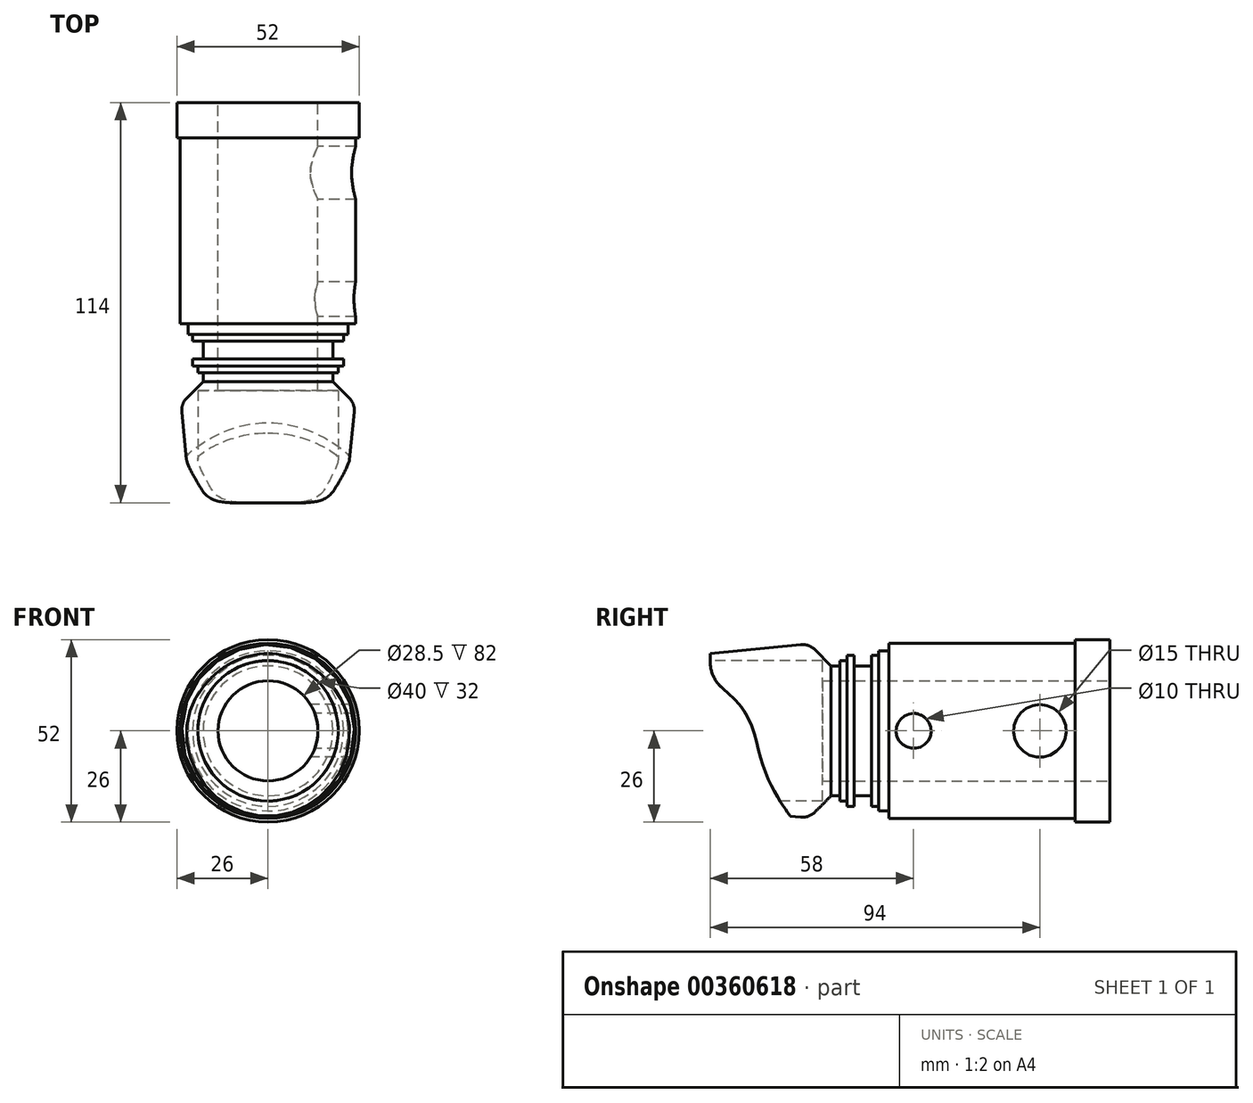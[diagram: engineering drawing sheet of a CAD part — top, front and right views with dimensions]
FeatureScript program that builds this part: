
annotation { "Feature Type Name" : "Feature", "Feature Type Description" : "" }
export const myFeature = defineFeature(function(context is Context, id is Id, definition is map)
    precondition{}
    {
        {
            var Q0;
            Q0=qCreatedBy(makeId("Front.planeOp"),FACE);
            var sketch = newSketch(context, id + "F0", { "sketchPlane" : qUnion([Q0])});
            skCircle(sketch, "E0", {"center": v(0, 0) * mm, "radius": 25 * mm});
            skSolve(sketch);
        }
        {
            var Q0;
            Q0 = qSketchRegion(id + "F0", true);
            extrude(context, id + "F1", {"entities" : qUnion([Q0]), "depth" : 53 * mm});
        }
        {
            var Q0;
            Q0=makeQuery(id+"F1.opExtrude","CAP_FACE",FACE,{"disambiguationData":[OSD([sQuery(id+"F0.wireOp",EDGE,"E0")])],"isStart":true});
            var sketch = newSketch(context, id + "F2", { "sketchPlane" : qUnion([Q0])});
            skCircle(sketch, "E1", {"center": v(0, 0) * mm, "radius": 26 * mm});
            skSolve(sketch);
        }
        {
            var Q0;
            Q0 = qSketchRegion(id + "F2", true);
            extrude(context, id + "F3", {"entities" : qUnion([Q0]), "operationType" : NewBodyOperationType.ADD, "depth" : 10 * mm});
        }
        {
            var Q0;
            Q0=makeQuery(id+"F1.opExtrude","CAP_FACE",FACE,{"disambiguationData":[OSD([sQuery(id+"F0.wireOp",EDGE,"E0")])],"isStart":false});
            var sketch = newSketch(context, id + "F4", { "sketchPlane" : qUnion([Q0])});
            skCircle(sketch, "E2", {"center": v(0, 0) * mm, "radius": 22.83 * mm});
            skSolve(sketch);
        }
        {
            var Q0;
            Q0 = qSketchRegion(id + "F4", true);
            extrude(context, id + "F5", {"entities" : qUnion([Q0]), "operationType" : NewBodyOperationType.ADD, "depth" : 3 * mm});
        }
        {
            var Q0;
            Q0=makeQuery(id+"F5.opExtrude","CAP_FACE",FACE,{"disambiguationData":[OSD([sQuery(id+"F4.wireOp",EDGE,"E2")])],"isStart":false});
            var sketch = newSketch(context, id + "F6", { "sketchPlane" : qUnion([Q0])});
            skCircle(sketch, "E3", {"center": v(0, 0) * mm, "radius": 21.5 * mm});
            skSolve(sketch);
        }
        {
            var Q0;
            Q0=makeQuery(id+"F6.imprint","IMPRINT",FACE,{"disambiguationData":[TD([[makeQuery(id+"F6.imprint","IMPRINT",EDGE,{"derivedFrom":sQuery(id+"F6.wireOp",EDGE,"E3")}),1.0]])]});
            extrude(context, id + "F7", {"entities" : qUnion([Q0]), "operationType" : NewBodyOperationType.ADD, "depth" : 2 * mm});
        }
        {
            var Q0;
            Q0=makeQuery(id+"F7.opExtrude","CAP_FACE",FACE,{"disambiguationData":[OSD([sQuery(id+"F6.wireOp",EDGE,"E3")])],"isStart":false});
            var sketch = newSketch(context, id + "F8", { "sketchPlane" : qUnion([Q0])});
            skCircle(sketch, "E4", {"center": v(0, 0) * mm, "radius": 18.5 * mm});
            skSolve(sketch);
        }
        {
            var Q0;
            Q0=makeQuery(id+"F8.imprint","IMPRINT",FACE,{"disambiguationData":[TD([[makeQuery(id+"F8.imprint","IMPRINT",EDGE,{"derivedFrom":sQuery(id+"F8.wireOp",EDGE,"E4")}),1.0]])]});
            extrude(context, id + "F9", {"entities" : qUnion([Q0]), "operationType" : NewBodyOperationType.ADD, "depth" : 5 * mm});
        }
        {
            var Q0;
            Q0=makeQuery(id+"F9.opExtrude","CAP_FACE",FACE,{"disambiguationData":[OSD([sQuery(id+"F8.wireOp",EDGE,"E4")])],"isStart":false});
            var sketch = newSketch(context, id + "F10", { "sketchPlane" : qUnion([Q0])});
            skCircle(sketch, "E5", {"center": v(0, 0) * mm, "radius": 21.5 * mm});
            skSolve(sketch);
        }
        {
            var Q0;
            Q0 = qSketchRegion(id + "F10", true);
            extrude(context, id + "F11", {"entities" : qUnion([Q0]), "operationType" : NewBodyOperationType.ADD, "depth" : 2 * mm});
        }
        {
            var Q0;
            Q0=makeQuery(id+"F11.opExtrude","CAP_FACE",FACE,{"disambiguationData":[OSD([sQuery(id+"F10.wireOp",EDGE,"E5")])],"isStart":false});
            var sketch = newSketch(context, id + "F12", { "sketchPlane" : qUnion([Q0])});
            skCircle(sketch, "E6", {"center": v(0, 0) * mm, "radius": 20 * mm});
            skSolve(sketch);
        }
        {
            var Q0;
            Q0 = qSketchRegion(id + "F12", true);
            extrude(context, id + "F13", {"entities" : qUnion([Q0]), "operationType" : NewBodyOperationType.ADD, "depth" : 2 * mm});
        }
        {
            var Q0;
            Q0=makeQuery(id+"F13.opExtrude","CAP_FACE",FACE,{"disambiguationData":[OSD([sQuery(id+"F12.wireOp",EDGE,"E6")])],"isStart":false});
            var sketch = newSketch(context, id + "F14", { "sketchPlane" : qUnion([Q0])});
            skCircle(sketch, "E7", {"center": v(0, 0) * mm, "radius": 18.5 * mm});
            skSolve(sketch);
        }
        {
            var Q0;
            Q0 = qSketchRegion(id + "F14", true);
            extrude(context, id + "F15", {"entities" : qUnion([Q0]), "operationType" : NewBodyOperationType.ADD, "depth" : 2 * mm});
        }
        {
            var Q0;
            Q0=makeQuery(id+"F15.opExtrude","CAP_FACE",FACE,{"disambiguationData":[OSD([sQuery(id+"F14.wireOp",EDGE,"E7")])],"isStart":false});
            var sketch = newSketch(context, id + "F16", { "sketchPlane" : qUnion([Q0])});
            skCircle(sketch, "E8", {"center": v(0, 0) * mm, "radius": 25 * mm});
            skSolve(sketch);
        }
        {
            var Q0;
            Q0 = qSketchRegion(id + "F16", true);
            extrude(context, id + "F17", {"entities" : qUnion([Q0]), "operationType" : NewBodyOperationType.ADD, "depth" : 35 * mm});
        }
        {
            var Q0;
            Q0=makeQuery(id+"F17.opExtrude","CAP_FACE",FACE,{"disambiguationData":[OSD([sQuery(id+"F16.wireOp",EDGE,"E8")])],"isStart":false});
            var sketch = newSketch(context, id + "F18", { "sketchPlane" : qUnion([Q0])});
            skCircle(sketch, "E9", {"center": v(0, 0) * mm, "radius": 20 * mm});
            skSolve(sketch);
        }
        {
            var Q0;
            Q0 = qSketchRegion(id + "F18", true);
            extrude(context, id + "F19", {"entities" : qUnion([Q0]), "operationType" : NewBodyOperationType.REMOVE, "oppositeDirection" : true, "depth" : 32 * mm});
        }
        {
            var Q0;
            Q0=makeQuery(id+"F17.opExtrude","CAP_EDGE",EDGE,{"disambiguationData":[OSD([sQuery(id+"F16.wireOp",EDGE,"E8")])],"isStart":true});
            chamfer(context, id + "F20", {"entities" : qUnion([Q0]), "width" : 7 * mm, "tangentPropagation" : true});
        }
        {
            var Q0;
            Q0=makeQuery(id+"F17.opExtrude","CAP_EDGE",EDGE,{"disambiguationData":[OSD([sQuery(id+"F16.wireOp",EDGE,"E8")])],"isStart":false});
            chamfer(context, id + "F21", {"entities" : qUnion([Q0]), "chamferType" : ChamferType.TWO_OFFSETS, "width1" : 3 * mm, "oppositeDirection" : false, "width2" : 30 * mm, "tangentPropagation" : true});
        }
        {
            var Q0;
            {var subQ0=sQuery(id+"F16.wireOp",EDGE,"E8");Q0=makeQuery(id+"F21.opChamfer","BLEND_EDGE",EDGE,{"blendedFrom":[makeQuery(id+"F17.opExtrude","CAP_EDGE",EDGE,{"disambiguationData":[OSD([subQ0])],"isStart":false}),makeQuery(id+"F20.opChamfer","BLEND_FACE",FACE,{"disambiguationData":[OSD([subQ0])]})],"blendedInto":[makeQuery(id+"F20.opChamfer","BLEND_FACE",FACE,{"disambiguationData":[OSD([subQ0])]})]});}
            fillet(context, id + "F22", {"entities" : qUnion([Q0]), "radius" : 5 * mm, "tangentPropagation" : true, "allowEdgeOverflow" : false});
        }
        {
            var Q0;
            Q0=qCreatedBy(makeId("Right.planeOp"),FACE);
            cPlane(context, id + "F23", {"entities" : qUnion([Q0]), "cplaneType" : CPlaneType.OFFSET, "offset" : 26.9 * mm, "width" : 150 * mm, "height" : 150 * mm});
        }
        {
            var Q0;
            Q0=qCreatedBy(id+"F23.planeOp",FACE);
            var sketch = newSketch(context, id + "F24", { "sketchPlane" : qUnion([Q0])});
            skLineSegment(sketch, "E10", {"start": v(0, 0) * mm, "end": v(-78, 0) * mm});
            skLineSegment(sketch, "E11", {"start": v(-78, 0) * mm, "end": v(-78, -31.05) * mm});
            skFitSpline(sketch, "E12", {"points": [v(-78, -28.4) * mm, v(-107.4, 17.05) * mm], "startDerivative": vector(-61.86, 75.7) * mm, "endDerivative": vector(-74.86, 47.26) * mm});
            skLineSegment(sketch, "E13", {"start": v(-78, -31.05) * mm, "end": v(-107.4, -31.05) * mm});
            skLineSegment(sketch, "E14", {"start": v(-107.4, -31.05) * mm, "end": v(-107.4, 17.05) * mm});
            skSolve(sketch);
        }
        {
            var Q0;
            {var subQ2=sQuery(id+"F24.wireOp",EDGE,"E12");Q0=makeQuery(id+"F24.imprint","IMPRINT",FACE,{"disambiguationData":[TD([[makeQuery(id+"F24.imprint","IMPRINT",EDGE,{"derivedFrom":subQ2}),1.0]])]});}
            extrude(context, id + "F25", {"entities" : qUnion([Q0]), "operationType" : NewBodyOperationType.REMOVE, "oppositeDirection" : true, "depth" : 52.3 * mm});
        }
        {
            var Q0;
            Q0=makeQuery(id+"F25.boolean.opBoolean","INTERSECT",EDGE,{"derivedFrom":[makeQuery(id+"F17.opExtrude","CAP_FACE",FACE,{"disambiguationData":[OSD([sQuery(id+"F16.wireOp",EDGE,"E8")])],"isStart":false}),makeQuery(id+"F25.opExtrude","SWEPT_FACE",FACE,{"disambiguationData":[OSD([sQuery(id+"F24.wireOp",EDGE,"E12")])]})]});
            fillet(context, id + "F26", {"entities" : qUnion([Q0]), "radius" : 10 * mm, "tangentPropagation" : true, "allowEdgeOverflow" : false});
        }
        {
            var Q0;
            Q0=makeQuery(id+"F3.opExtrude","CAP_FACE",FACE,{"disambiguationData":[OSD([sQuery(id+"F2.wireOp",EDGE,"E1")])],"isStart":false});
            var sketch = newSketch(context, id + "F27", { "sketchPlane" : qUnion([Q0])});
            skCircle(sketch, "E15", {"center": v(0, 0) * mm, "radius": 14.25 * mm});
            skSolve(sketch);
        }
        {
            var Q0;
            Q0 = qSketchRegion(id + "F27", true);
            extrude(context, id + "F28", {"entities" : qUnion([Q0]), "operationType" : NewBodyOperationType.REMOVE, "oppositeDirection" : true, "depth" : 128 * mm});
        }
        {
            var Q0;
            Q0=qCreatedBy(makeId("Right.planeOp"),FACE);
            var sketch = newSketch(context, id + "F29", { "sketchPlane" : qUnion([Q0])});
            skLineSegment(sketch, "E16", {"start": v(0, 0) * mm, "end": v(-10, 0) * mm});
            skCircle(sketch, "E17", {"center": v(-10, 0) * mm, "radius": 7.5 * mm});
            skLineSegment(sketch, "E18", {"start": v(-10, 0) * mm, "end": v(-46, 0) * mm});
            skCircle(sketch, "E19", {"center": v(-46, 0) * mm, "radius": 5 * mm});
            skSolve(sketch);
        }
        {
            var Q0;
            Q0 = qSketchRegion(id + "F29", true);
            extrude(context, id + "F30", {"entities" : qUnion([Q0]), "operationType" : NewBodyOperationType.REMOVE, "depth" : 39.2 * mm});
        }
    });
